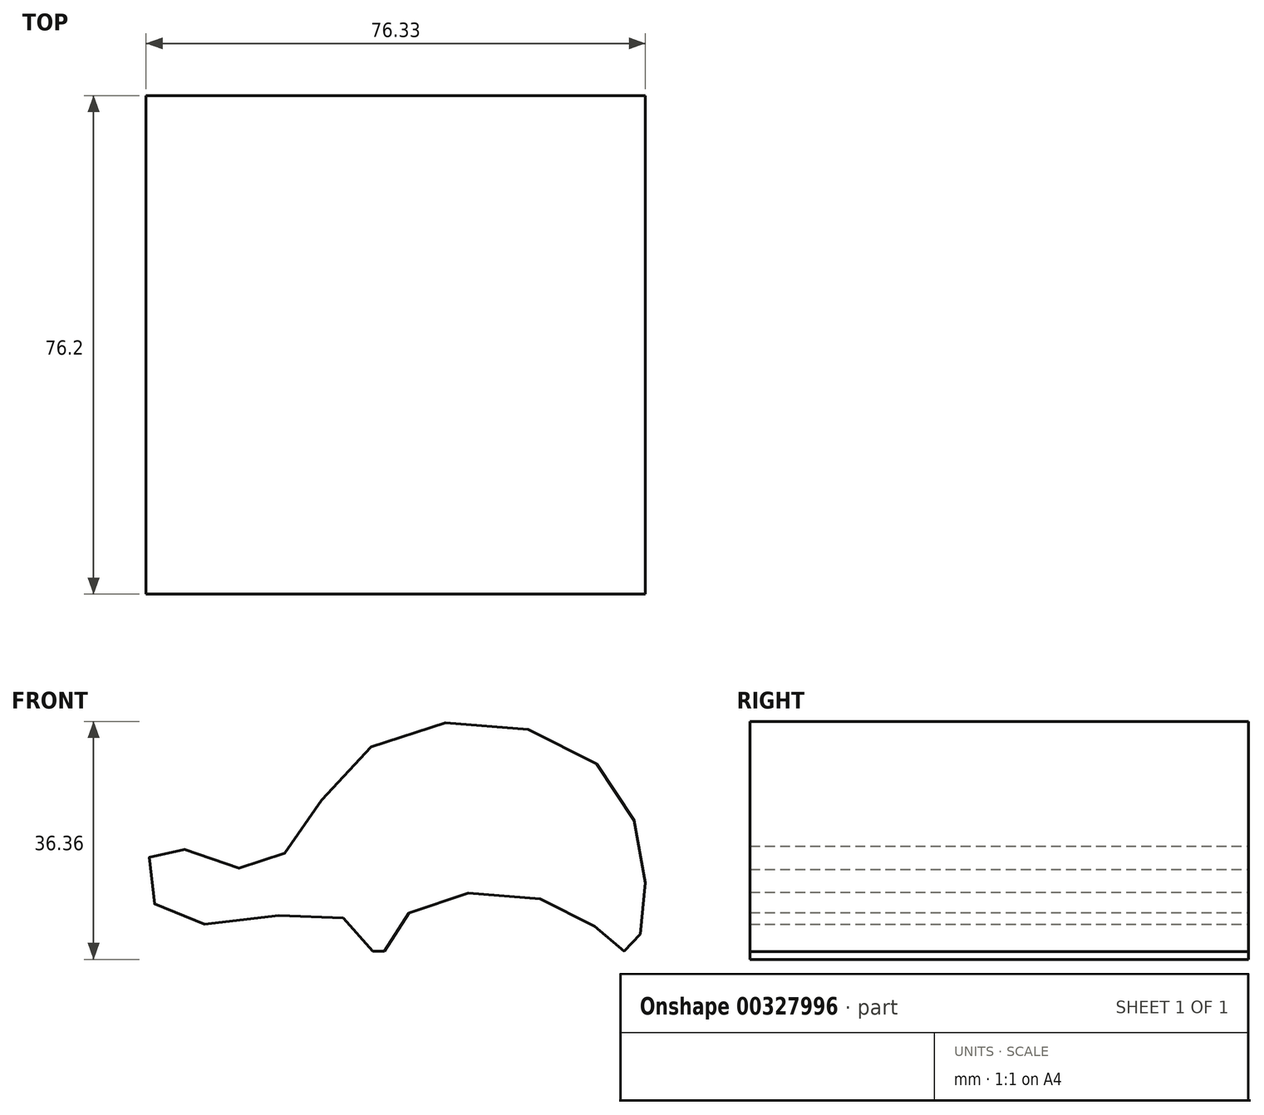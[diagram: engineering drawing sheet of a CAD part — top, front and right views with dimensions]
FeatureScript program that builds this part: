
annotation { "Feature Type Name" : "Feature", "Feature Type Description" : "" }
export const myFeature = defineFeature(function(context is Context, id is Id, definition is map)
    precondition{}
    {
        {
            var Q0;
            Q0=qCreatedBy(makeId("Front.planeOp"),FACE);
            var sketch = newSketch(context, id + "F0", { "sketchPlane" : qUnion([Q0])});
            skFitSpline(sketch, "E0", {"points": [v(5.76, 23.89) * mm, v(11.22, 17.56) * mm, v(15.25, 24.18) * mm, v(40.58, 25.04) * mm, v(49.21, 18.7) * mm, v(51.8, 25.33) * mm, v(44.03, 47.78) * mm, v(9.2, 49.5) * mm, v(-7.2, 31.37) * mm, v(-22.74, 34.54) * mm, v(-21.3, 24.18) * mm, v(5.76, 23.89) * mm]});
            skSolve(sketch);
        }
        {
            var Q0;
            Q0=makeQuery(id+"F0.imprint","IMPRINT",FACE,{"disambiguationData":[TD([[makeQuery(id+"F0.imprint","IMPRINT",EDGE,{"derivedFrom":sQuery(id+"F0.wireOp",EDGE,"E0")}),1.0]])]});
            extrude(context, id + "F1", {"entities" : qUnion([Q0]), "depth" : 76.2 * mm});
        }
    });
